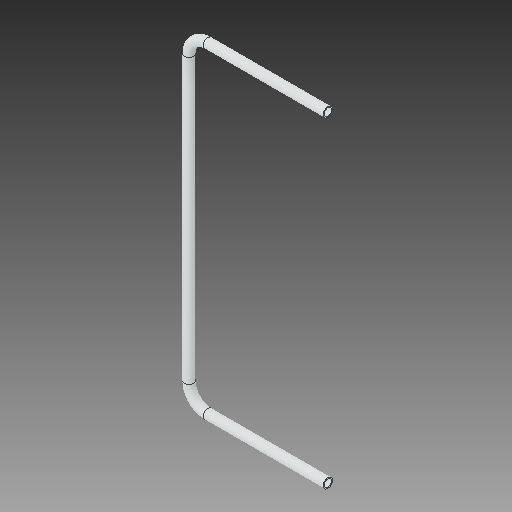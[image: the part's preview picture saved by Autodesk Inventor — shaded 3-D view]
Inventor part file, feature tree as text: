
AUTODESK INVENTOR PART (.ipt)
format: ipt  version: 2018 (Build 220112000, 112)  size: 102,400 bytes
history: native  units: in
note: dims shown in document units (in); Inventor stores cm internally (conversion verified against a paired STEP export)
features: sweep x1
ambient origin geometry x8: Origin, YZ Plane, XZ Plane, XY Plane, X Axis, Y Axis, Z Axis, Center Point
bodies: Solid1 (feature_tree)
feature tree (1):
  sweep  "Sweep1"
